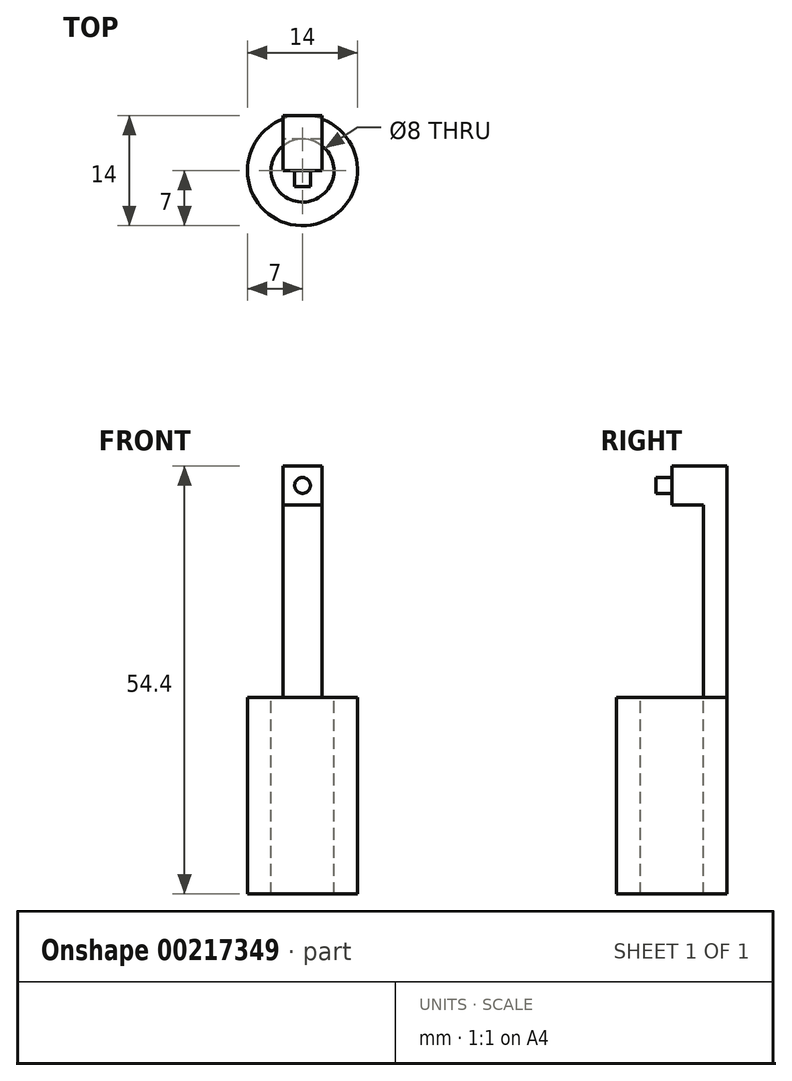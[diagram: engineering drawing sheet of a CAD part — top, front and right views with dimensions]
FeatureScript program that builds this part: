
annotation { "Feature Type Name" : "Feature", "Feature Type Description" : "" }
export const myFeature = defineFeature(function(context is Context, id is Id, definition is map)
    precondition{}
    {
        {
            var Q0;
            Q0=qCreatedBy(makeId("Front.planeOp"),FACE);
            var sketch = newSketch(context, id + "F0", { "sketchPlane" : qUnion([Q0])});
            skLineSegment(sketch, "E0.bottom", {"start": v(2.5, 2.5) * mm, "end": v(-2.5, 2.5) * mm});
            skLineSegment(sketch, "E0.top", {"start": v(2.5, -2.5) * mm, "end": v(-2.5, -2.5) * mm});
            skLineSegment(sketch, "E0.left", {"start": v(2.5, 2.5) * mm, "end": v(2.5, -2.5) * mm});
            skLineSegment(sketch, "E0.right", {"start": v(-2.5, 2.5) * mm, "end": v(-2.5, -2.5) * mm});
            skPoint(sketch, "E0.middle", {"position": v(0, 0) * mm});
            skSolve(sketch);
        }
        {
            var Q0;
            Q0=makeQuery(id+"F0.imprint","IMPRINT",FACE,{"disambiguationData":[TD([[makeQuery(id+"F0.imprint","IMPRINT",EDGE,{"derivedFrom":sQuery(id+"F0.wireOp",EDGE,"E0.bottom")}),1.0]])]});
            extrude(context, id + "F1", {"entities" : qUnion([Q0]), "depth" : 4 * mm});
        }
        {
            var Q0;
            Q0=makeQuery(id+"F1.opExtrude","CAP_FACE",FACE,{"disambiguationData":[OSD([sQuery(id+"F0.wireOp",EDGE,"E0.bottom"),sQuery(id+"F0.wireOp",EDGE,"E0.top"),sQuery(id+"F0.wireOp",EDGE,"E0.left"),sQuery(id+"F0.wireOp",EDGE,"E0.right")])],"isStart":false});
            var sketch = newSketch(context, id + "F2", { "sketchPlane" : qUnion([Q0])});
            skCircle(sketch, "E1", {"center": v(0, 0) * mm, "radius": 1 * mm});
            skSolve(sketch);
        }
        {
            var Q0;
            Q0=makeQuery(id+"F2.imprint","IMPRINT",FACE,{"disambiguationData":[TD([[makeQuery(id+"F2.imprint","IMPRINT",EDGE,{"derivedFrom":sQuery(id+"F2.wireOp",EDGE,"E1")}),1.0]])]});
            extrude(context, id + "F3", {"entities" : qUnion([Q0]), "operationType" : NewBodyOperationType.ADD, "depth" : 2 * mm});
        }
        {
            var Q0;
            Q0=makeQuery(id+"F1.opExtrude","CAP_FACE",FACE,{"disambiguationData":[OSD([sQuery(id+"F0.wireOp",EDGE,"E0.bottom"),sQuery(id+"F0.wireOp",EDGE,"E0.top"),sQuery(id+"F0.wireOp",EDGE,"E0.left"),sQuery(id+"F0.wireOp",EDGE,"E0.right")])],"isStart":true});
            var sketch = newSketch(context, id + "F4", { "sketchPlane" : qUnion([Q0])});
            skLineSegment(sketch, "E2.bottom", {"start": v(-2.5, 2.5) * mm, "end": v(2.5, 2.5) * mm});
            skLineSegment(sketch, "E2.top", {"start": v(-2.5, -26.9) * mm, "end": v(2.5, -26.9) * mm});
            skLineSegment(sketch, "E2.left", {"start": v(-2.5, 2.5) * mm, "end": v(-2.5, -26.9) * mm});
            skLineSegment(sketch, "E2.right", {"start": v(2.5, 2.5) * mm, "end": v(2.5, -26.9) * mm});
            skSolve(sketch);
        }
        {
            var Q0;
            {var subQ0=sQuery(id+"F4.wireOp",EDGE,"E2.top");Q0=makeQuery(id+"F4.imprint","IMPRINT",FACE,{"disambiguationData":[TD([[makeQuery(id+"F4.imprint","IMPRINT",EDGE,{"derivedFrom":subQ0}),1.0]])]});}
            var Q1;
            {var subQ0=sQuery(id+"F4.wireOp",EDGE,"E2.bottom");Q1=makeQuery(id+"F4.imprint","IMPRINT",FACE,{"disambiguationData":[TD([[makeQuery(id+"F4.imprint","IMPRINT",EDGE,{"derivedFrom":subQ0}),-1.0]])]});}
            extrude(context, id + "F5", {"entities" : qUnion([Q0, Q1]), "operationType" : NewBodyOperationType.ADD, "depth" : 3 * mm});
        }
        {
            var Q0;
            Q0=makeQuery(id+"F5.opExtrude","SWEPT_FACE",FACE,{"disambiguationData":[OSD([sQuery(id+"F4.wireOp",EDGE,"E2.top")])]});
            var sketch = newSketch(context, id + "F6", { "sketchPlane" : qUnion([Q0])});
            skCircle(sketch, "E3", {"center": v(0, 4) * mm, "radius": 4 * mm});
            skLineSegment(sketch, "E4", {"start": v(0, 4) * mm, "end": v(4.2, 4) * mm});
            skCircle(sketch, "E5", {"center": v(0, 4) * mm, "radius": 7 * mm});
            skSolve(sketch);
        }
        {
            var Q0;
            {var subQ8=sQuery(id+"F6.wireOp",EDGE,"E3");var subQ9=makeQuery(id+"F6.imprint","IMPRINT",VERTEX,{"derivedFrom":subQ8});Q0=makeQuery(id+"F6.imprint","IMPRINT",FACE,{"disambiguationData":[TD([[makeQuery(id+"F6.imprint","IMPRINT",EDGE,{"disambiguationData":[TD([[subQ9,-1.0]])],"derivedFrom":subQ8}),-1.0]])]});}
            var Q1;
            {var subQ0=sQuery(id+"F4.wireOp",EDGE,"E2.top");var subQ4=sQuery(id+"F6.wireOp",EDGE,"E5");var subQ9=makeQuery(id+"F6.imprint","INTERSECT",VERTEX,{"derivedFrom":[makeQuery(id+"F5.opExtrude","CAP_EDGE",EDGE,{"disambiguationData":[OSD([subQ0])],"isStart":false}),subQ4]});Q1=makeQuery(id+"F6.imprint","IMPRINT",FACE,{"disambiguationData":[TD([[makeQuery(id+"F6.imprint","IMPRINT",EDGE,{"disambiguationData":[TD([[subQ9,1.0]])],"derivedFrom":subQ4}),1.0]])]});}
            extrude(context, id + "F7", {"entities" : qUnion([Q0, Q1]), "depth" : 25 * mm});
        }
    });
